# Revit family: IS_Connect_E5674_BIM_DE
name_source: partatom
category: Plumbing Fixtures
revit_build: Autodesk Revit MEP 2016 (Build: 20161004_0715(x64)
units: mm (PartAtom-declared; Revit-internal decimal feet)

## family parameters
Always vertical = No
Cut with Voids When Loaded = No
OmniClass Number = 23.45.05.21.11.21
OmniClass Title = Urinals
Part Type = Normal
Room Calculation Point = No
Round Connector Dimension = Use Diameter
Shared = No
Work Plane-Based = No

## types (1)
- E567401 CONNECT urinal cover
    Accessories = www.idealstandard.de\ersatzteile
    AreaUnits = millimeters
    AssetType = Fixed
    BIMObjectName = ISI_IdealStandard_WallHungUrinals_Connect_E567401
    BIMobject category = Urinals
    BOSUseNativeGeometries = 1
    BarCode = 5017830480570
    Brand = Ideal Standard
    Brand url = http://www.idealstandard.co.uk
    CodePerformance = 0
    Color = White
    ConnectionType = Plumbing
    Cost = 0 $
    CurrencyUnit = €
    CurrentRevision = 1
    Date of publishing = 2017_11_20
    Description = E567401 CONNECT urinal cover
    DurationUnit = year
    EAN code = 5017830480570
    Edition number = 1
    ExpectedLife = 25
    Features = CONNECT urinal cover
    Finish = White
    IFC Classification = Sanitary Terminal
    IfcExportAs = IfcSanitaryTerminalType
    IfcExportType = URINALS
    Installation instructions = http://www.idealstandard.de
    InstallationInstructions = www.idealstandard.de\produkte
    LinearUnits = millimeters
    MainColor = White
    Manufacturer name = Ideal Standard
    ManufacturerURL = www.idealstandard.com
    Material = Duroplast
    Model = E567401
    ModelNumber = E567401
    ModelReference = E567401 CONNECT urinal cover
    NBS Reference Code = 35-93-82
    NBS Reference Description = Wall-Hung Urinals
    Name = WallHungUrinals_Connect_E567401_IdealStandard
    NettWeight = 0,9 kg
    Nominal height = 0
    Nominal width = 0
    NominalDepth = 306 mm  [stored 1.00394 ft]
    NominalHeight = 38 mm
    NominalLength = 306 mm  [stored 1.00394 ft]
    NominalWidth = 265 mm
    OmniClass Code = 23-31 21 00
    OmniClass Description = Urinals
    Product Guid = c03b0ae4-f323-4b96-b961-a0a36ff7a5f8
    Product SKU = E5674
    Product data url = https://bimobject.com
    Product family = CONNECT
    Product group = Urinal
    Product name = CONNECT urinal cover
    Product url = http://www.idealstandard.de
    ProductInformation = www.idealstandard.de/produkte
    QR code = http://bimobject.com
    Shape = Sculptured
    Space = Internal
    SpareParts = www.idealstandard.de/ersatzteile
    SpilloverLevel = 0 mm  [stored 0 ft]
    Technical description = http://www.idealstandard.de
    URL = http://www.idealstandard.de
    Uniclass 1.4 Code = L7217
    Uniclass 1.4 Description = Urinals
    Uniclass 2.0 Code = PR-35-93-82
    Uniclass 2.0 Description = Wall-Hung Urinals
    Uniclass 2015 Code = Pr_40_20_93_82
    Uniclass 2015 Name = Wall-hung urinals
    Uniclass2015Code = Pr_40_20_93_82
    Uniclass2015Title = Wall-hung urinals
    Uniclass2015Version = Products v1.1
    UrinalColor = White
    UrinalMaterial = Duroplast
    Version = 1
    VolumeUnits = Litres
    Weight Net (Kg) = 0.9

note: [stored X ft] marks values corroborated as IEEE doubles in the binary element streams (Revit-internal decimal feet)

## geometry (parser evidence)
native form markers: Blend x4, Sweep x1
no freeform markers — native parametric forms only
